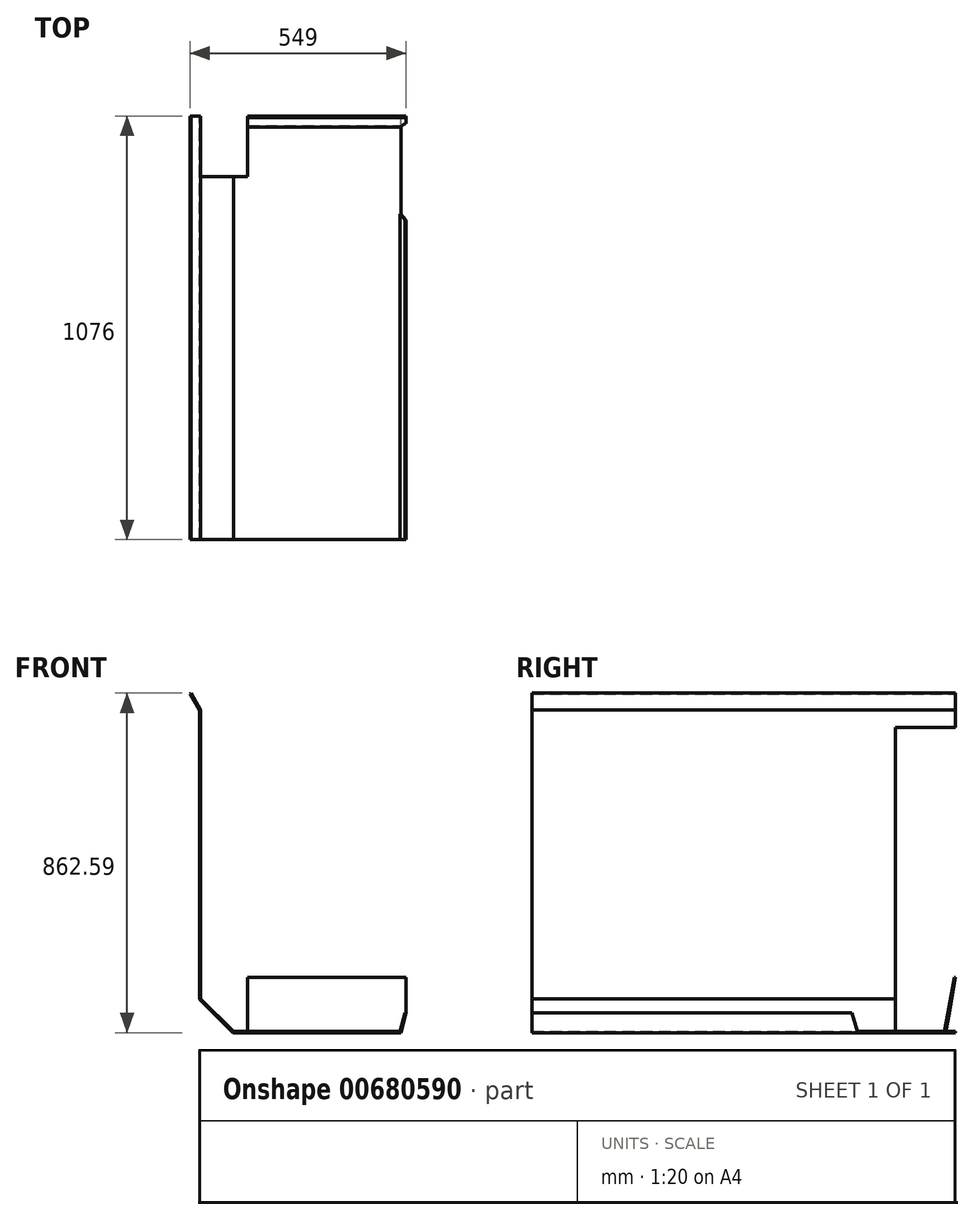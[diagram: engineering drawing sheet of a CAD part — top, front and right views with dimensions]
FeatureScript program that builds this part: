
annotation { "Feature Type Name" : "Feature", "Feature Type Description" : "" }
export const myFeature = defineFeature(function(context is Context, id is Id, definition is map)
    precondition{}
    {
        {
            var Q0;
            Q0=qCreatedBy(makeId("Front.planeOp"),FACE);
            var sketch = newSketch(context, id + "F0", { "sketchPlane" : qUnion([Q0])});
            skLineSegment(sketch, "E0", {"start": v(0, 85) * mm, "end": v(0, 819) * mm});
            skLineSegment(sketch, "E1", {"start": v(0, 819) * mm, "end": v(-24, 861) * mm});
            skLineSegment(sketch, "E2.0", {"start": v(3.2, 819.85) * mm, "end": v(-21.22, 862.59) * mm});
            skLineSegment(sketch, "E3", {"start": v(-24, 861) * mm, "end": v(-21.22, 862.59) * mm});
            skLineSegment(sketch, "E4", {"start": v(85, 0) * mm, "end": v(512, 0) * mm});
            skLineSegment(sketch, "E5", {"start": v(512, 0) * mm, "end": v(525, 50) * mm});
            skLineSegment(sketch, "E6.0", {"start": v(509.53, 3.2) * mm, "end": v(521.9, 50.8) * mm});
            skLineSegment(sketch, "E7", {"start": v(521.9, 50.8) * mm, "end": v(525, 50) * mm});
            skLineSegment(sketch, "E8", {"start": v(0, 85) * mm, "end": v(85, 0) * mm});
            skLineSegment(sketch, "E9.0", {"start": v(3.2, 86.33) * mm, "end": v(86.33, 3.2) * mm});
            skLineSegment(sketch, "E10.trimOffspring", {"start": v(86.33, 3.2) * mm, "end": v(509.53, 3.2) * mm});
            skLineSegment(sketch, "E11.trimOffspring", {"start": v(3.2, 86.33) * mm, "end": v(3.2, 819.85) * mm});
            skPoint(sketch, "E12.orphan", {"position": v(0, 0) * mm});
            skSolve(sketch);
        }
        {
            var Q0;
            Q0 = qSketchRegion(id + "F0", true);
            extrude(context, id + "F1", {"entities" : qUnion([Q0]), "depth" : 1076 * mm, "offsetDistance" : 25 * mm});
        }
        {
            var Q0;
            Q0=makeQuery(id+"F1.opExtrude","CAP_FACE",FACE,{"disambiguationData":[OSD([sQuery(id+"F0.wireOp",EDGE,"E0"),sQuery(id+"F0.wireOp",EDGE,"E1"),sQuery(id+"F0.wireOp",EDGE,"E2.0"),sQuery(id+"F0.wireOp",EDGE,"E3"),sQuery(id+"F0.wireOp",EDGE,"E4"),sQuery(id+"F0.wireOp",EDGE,"E5"),sQuery(id+"F0.wireOp",EDGE,"E6.0"),sQuery(id+"F0.wireOp",EDGE,"E7"),sQuery(id+"F0.wireOp",EDGE,"E8"),sQuery(id+"F0.wireOp",EDGE,"E9.0"),sQuery(id+"F0.wireOp",EDGE,"E10.trimOffspring"),sQuery(id+"F0.wireOp",EDGE,"E11.trimOffspring")])],"isStart":true});
            var sketch = newSketch(context, id + "F2", { "sketchPlane" : qUnion([Q0])});
            skLineSegment(sketch, "E13.bottom", {"start": v(0, 0) * mm, "end": v(-123, 0) * mm});
            skLineSegment(sketch, "E13.top", {"start": v(0, 775) * mm, "end": v(-123, 775) * mm});
            skLineSegment(sketch, "E13.left", {"start": v(0, 0) * mm, "end": v(0, 775) * mm});
            skLineSegment(sketch, "E13.right", {"start": v(-123, 0) * mm, "end": v(-123, 775) * mm});
            skSolve(sketch);
        }
        {
            var Q0;
            Q0 = qSketchRegion(id + "F2", true);
            extrude(context, id + "F3", {"entities" : qUnion([Q0]), "operationType" : NewBodyOperationType.REMOVE, "oppositeDirection" : true, "depth" : 153 * mm, "offsetDistance" : 25 * mm});
        }
        {
            var Q0;
            Q0=makeQuery(id+"F3.boolean.opBoolean","COPY",FACE,{"derivedFrom":makeQuery(id+"F3.opExtrude","SWEPT_FACE",FACE,{"disambiguationData":[OSD([sQuery(id+"F2.wireOp",EDGE,"E13.right")])]})});
            var sketch = newSketch(context, id + "F4", { "sketchPlane" : qUnion([Q0])});
            skLineSegment(sketch, "E14", {"start": v(25, 0) * mm, "end": v(0, 140) * mm});
            skLineSegment(sketch, "E15.0", {"start": v(28.15, 0.56) * mm, "end": v(3.15, 140.56) * mm});
            skLineSegment(sketch, "E16", {"start": v(0, 140) * mm, "end": v(3.15, 140.56) * mm});
            skLineSegment(sketch, "E17", {"start": v(25, 0) * mm, "end": v(28.15, 0.56) * mm});
            skSolve(sketch);
        }
        {
            var Q0;
            Q0 = qSketchRegion(id + "F4", true);
            extrude(context, id + "F5", {"entities" : qUnion([Q0]), "operationType" : NewBodyOperationType.ADD, "oppositeDirection" : true, "depth" : (525 - 123) * mm, "offsetDistance" : 25 * mm});
        }
        {
            var Q0;
            Q0=makeQuery(id+"F1.opExtrude","SWEPT_FACE",FACE,{"disambiguationData":[OSD([sQuery(id+"F0.wireOp",EDGE,"E6.0")])]});
            var sketch = newSketch(context, id + "F6", { "sketchPlane" : qUnion([Q0])});
            skLineSegment(sketch, "E18", {"start": v(0, 131.31) * mm, "end": v(249, 131.31) * mm});
            skLineSegment(sketch, "E19", {"start": v(263.76, 180.5) * mm, "end": v(249, 131.31) * mm});
            skLineSegment(sketch, "E20", {"start": v(24.43, 131.31) * mm, "end": v(15.93, 180.5) * mm});
            skLineSegment(sketch, "E21.0", {"start": v(27.68, 131.31) * mm, "end": v(19.08, 181.04) * mm});
            skLineSegment(sketch, "E22", {"start": v(0, 180.5) * mm, "end": v(263.76, 180.5) * mm});
            skSolve(sketch);
        }
        {
            var Q0;
            Q0 = qSketchRegion(id + "F6", true);
            var Q1;
            {var subQ1=sQuery(id+"F0.wireOp",EDGE,"E6.0");var subQ2=makeQuery(id+"F1.opExtrude","CAP_EDGE",EDGE,{"disambiguationData":[OSD([subQ1])],"isStart":true});Q1=makeQuery(id+"F6.imprint","IMPRINT",FACE,{"disambiguationData":[TD([[makeQuery(id+"F6.imprint","IMPRINT",EDGE,{"derivedFrom":subQ2}),-1.0]])]});}
            extrude(context, id + "F7", {"entities" : qUnion([Q0, Q1]), "operationType" : NewBodyOperationType.REMOVE, "oppositeDirection" : true, "depth" : 25 * mm, "offsetDistance" : 25 * mm});
        }
        {
            var Q0;
            {var subQ0=sQuery(id+"F0.wireOp",EDGE,"E7");var subQ1=sQuery(id+"F0.wireOp",EDGE,"E6.0");var subQ2=sQuery(id+"F0.wireOp",EDGE,"E5");var subQ3=sQuery(id+"F0.wireOp",EDGE,"E4");var subQ4=sQuery(id+"F0.wireOp",EDGE,"E10.trimOffspring");Q0=makeQuery(id+"F3.boolean.opBoolean","SPLIT",FACE,{"disambiguationData":[TD([makeQuery(id+"F1.opExtrude","SWEPT_FACE",FACE,{"disambiguationData":[OSD([subQ3])]})])],"derivedFrom":makeQuery(id+"F1.opExtrude","CAP_FACE",FACE,{"disambiguationData":[OSD([sQuery(id+"F0.wireOp",EDGE,"E0"),sQuery(id+"F0.wireOp",EDGE,"E1"),sQuery(id+"F0.wireOp",EDGE,"E2.0"),sQuery(id+"F0.wireOp",EDGE,"E3"),subQ3,subQ2,subQ1,subQ0,sQuery(id+"F0.wireOp",EDGE,"E8"),sQuery(id+"F0.wireOp",EDGE,"E9.0"),subQ4,sQuery(id+"F0.wireOp",EDGE,"E11.trimOffspring")])],"isStart":true})});}
            var sketch = newSketch(context, id + "F8", { "sketchPlane" : qUnion([Q0])});
            skLineSegment(sketch, "E23", {"start": v(-512, 0) * mm, "end": v(-513.43, 5.49) * mm});
            skLineSegment(sketch, "E24", {"start": v(-513.43, 5.49) * mm, "end": v(-525.58, 0) * mm});
            skLineSegment(sketch, "E25", {"start": v(-525.58, 0) * mm, "end": v(-512, 0) * mm});
            skSolve(sketch);
        }
        {
            var Q0;
            Q0 = qSketchRegion(id + "F8", true);
            extrude(context, id + "F9", {"entities" : qUnion([Q0]), "operationType" : NewBodyOperationType.REMOVE, "oppositeDirection" : true, "depth" : 50 * mm, "offsetDistance" : 25 * mm});
        }
        {
            var Q0;
            {var subQ0=sQuery(id+"F0.wireOp",EDGE,"E7");var subQ1=sQuery(id+"F0.wireOp",EDGE,"E6.0");var subQ2=sQuery(id+"F0.wireOp",EDGE,"E5");var subQ3=sQuery(id+"F0.wireOp",EDGE,"E4");var subQ4=sQuery(id+"F0.wireOp",EDGE,"E10.trimOffspring");Q0=makeQuery(id+"F3.boolean.opBoolean","SPLIT",FACE,{"disambiguationData":[TD([makeQuery(id+"F1.opExtrude","SWEPT_FACE",FACE,{"disambiguationData":[OSD([subQ3])]})])],"derivedFrom":makeQuery(id+"F1.opExtrude","CAP_FACE",FACE,{"disambiguationData":[OSD([sQuery(id+"F0.wireOp",EDGE,"E0"),sQuery(id+"F0.wireOp",EDGE,"E1"),sQuery(id+"F0.wireOp",EDGE,"E2.0"),sQuery(id+"F0.wireOp",EDGE,"E3"),subQ3,subQ2,subQ1,subQ0,sQuery(id+"F0.wireOp",EDGE,"E8"),sQuery(id+"F0.wireOp",EDGE,"E9.0"),subQ4,sQuery(id+"F0.wireOp",EDGE,"E11.trimOffspring")])],"isStart":true})});}
            var sketch = newSketch(context, id + "F10", { "sketchPlane" : qUnion([Q0])});
            skLineSegment(sketch, "E26", {"start": v(-509.53, 3.2) * mm, "end": v(-512.62, 3.2) * mm});
            skLineSegment(sketch, "E27", {"start": v(-512.62, 2.4) * mm, "end": v(-512.62, 3.2) * mm});
            skLineSegment(sketch, "E28", {"start": v(-512.62, 2.4) * mm, "end": v(-509.53, 3.2) * mm});
            skSolve(sketch);
        }
        {
            var Q0;
            Q0 = qSketchRegion(id + "F10", true);
            extrude(context, id + "F11", {"entities" : qUnion([Q0]), "operationType" : NewBodyOperationType.ADD, "oppositeDirection" : true, "depth" : 260 * mm, "offsetDistance" : 25 * mm});
        }
    });
